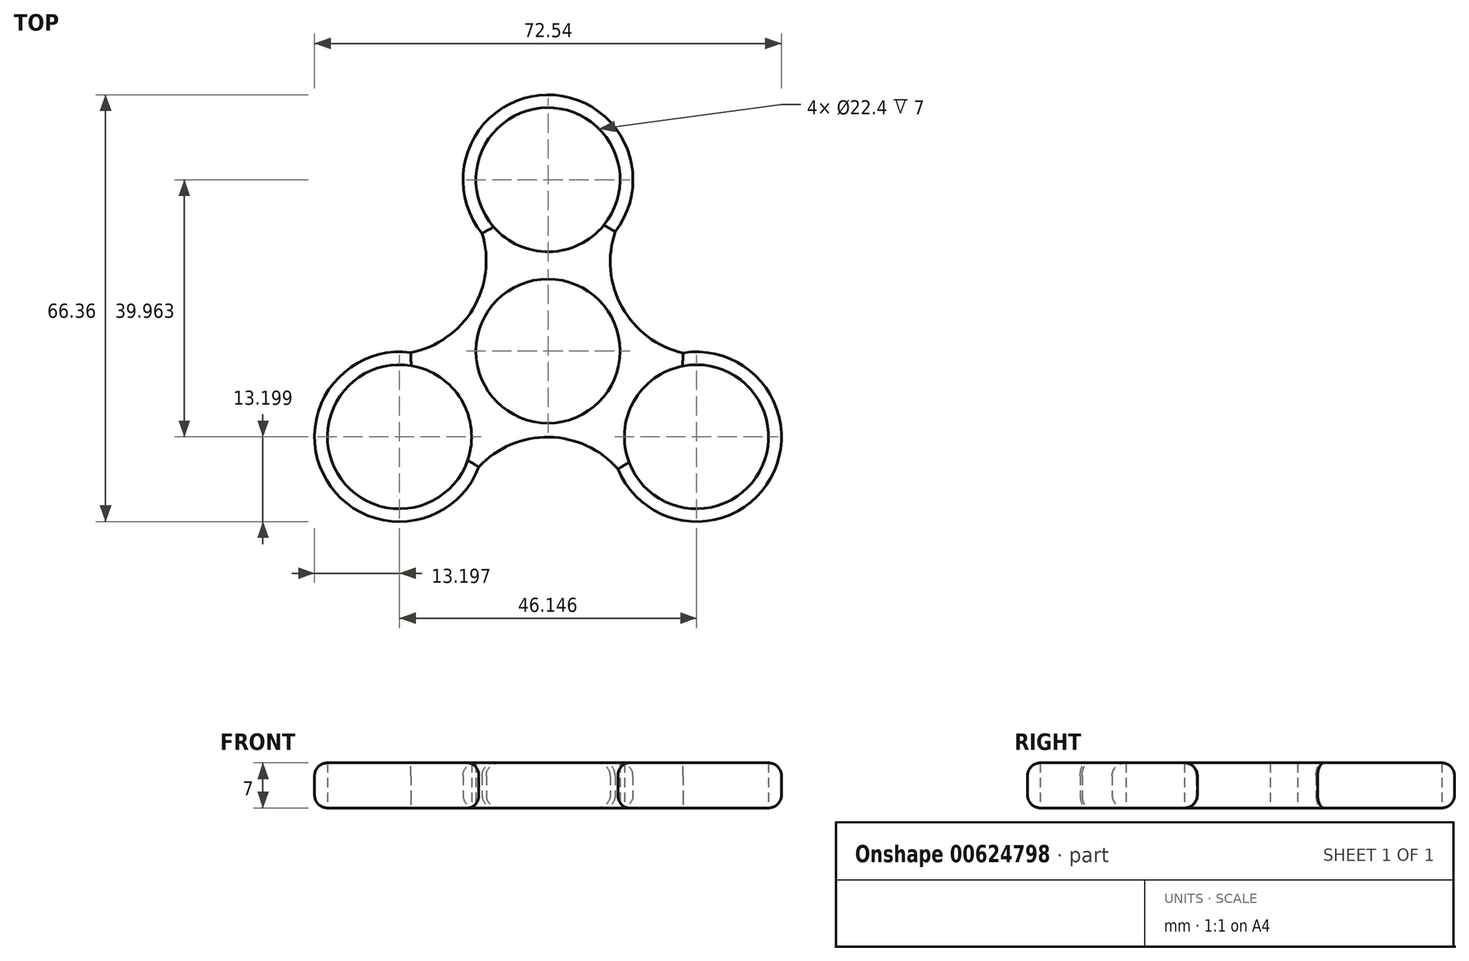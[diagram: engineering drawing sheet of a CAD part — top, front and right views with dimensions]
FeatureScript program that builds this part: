
annotation { "Feature Type Name" : "Feature", "Feature Type Description" : "" }
export const myFeature = defineFeature(function(context is Context, id is Id, definition is map)
    precondition{}
    {
        {
            var Q0;
            Q0=qCreatedBy(makeId("Top.planeOp"),FACE);
            var sketch = newSketch(context, id + "F0", { "sketchPlane" : qUnion([Q0])});
            skCircle(sketch, "E0", {"center": v(0, 0) * mm, "radius": 11.2 * mm});
            skCircle(sketch, "E1", {"center": v(0, 26.64) * mm, "radius": 11.2 * mm});
            skArc(sketch, "E2", {"start": v(10.45, 18.58) * mm, "mid": v(-0.17, 39.84) * mm, "end": v(-10.24, 18.3) * mm});
            skArc(sketch, "E3.1.0", {"start": v(-21.31, -0.24) * mm, "mid": v(-34.42, -20.07) * mm, "end": v(-10.74, -18.02) * mm});
            skCircle(sketch, "E3.1.1", {"center": v(-23.07, -13.32) * mm, "radius": 11.2 * mm});
            skArc(sketch, "E3.2.0", {"start": v(10.86, -18.34) * mm, "mid": v(34.59, -19.77) * mm, "end": v(20.98, -0.29) * mm});
            skCircle(sketch, "E3.2.1", {"center": v(23.07, -13.32) * mm, "radius": 11.2 * mm});
            skLineSegment(sketch, "E4", {"start": v(-13.37, -7.72) * mm, "end": v(-11.64, -6.72) * mm, "construction": true});
            skArc(sketch, "E5", {"start": v(10.45, 18.58) * mm, "mid": v(11.52, 6.8) * mm, "end": v(20.98, -0.29) * mm});
            skArc(sketch, "E6.1.0", {"start": v(-21.31, -0.24) * mm, "mid": v(-11.65, 6.57) * mm, "end": v(-10.24, 18.3) * mm});
            skArc(sketch, "E6.2.0", {"start": v(10.86, -18.34) * mm, "mid": v(0.13, -13.38) * mm, "end": v(-10.74, -18.02) * mm});
            skLineSegment(sketch, "E7.trimOffspring", {"start": v(11.54, 6.66) * mm, "end": v(23.07, -13.32) * mm, "construction": true});
            skLineSegment(sketch, "E8.trimOffspring", {"start": v(9.7, 5.6) * mm, "end": v(11.58, 6.69) * mm, "construction": true});
            skSolve(sketch);
        }
        {
            var Q0;
            Q0=makeQuery(id+"F0.imprint","IMPRINT",FACE,{"disambiguationData":[TD([[makeQuery(id+"F0.imprint","IMPRINT",EDGE,{"derivedFrom":sQuery(id+"F0.wireOp",EDGE,"E0")}),-1.0]])]});
            extrude(context, id + "F1", {"entities" : qUnion([Q0]), "depth" : 7 * mm, "offsetDistance" : 25 * mm});
        }
        {
            var Q0;
            Q0=makeQuery(id+"F1.opExtrude","CAP_EDGE",EDGE,{"disambiguationData":[OSD([sQuery(id+"F0.wireOp",EDGE,"E6.2.0")])],"isStart":true});
            var Q1;
            Q1=makeQuery(id+"F1.opExtrude","CAP_EDGE",EDGE,{"disambiguationData":[OSD([sQuery(id+"F0.wireOp",EDGE,"E3.2.0")])],"isStart":true});
            var Q2;
            Q2=makeQuery(id+"F1.opExtrude","CAP_EDGE",EDGE,{"disambiguationData":[OSD([sQuery(id+"F0.wireOp",EDGE,"E5")])],"isStart":true});
            var Q3;
            Q3=makeQuery(id+"F1.opExtrude","CAP_EDGE",EDGE,{"disambiguationData":[OSD([sQuery(id+"F0.wireOp",EDGE,"E2")])],"isStart":true});
            var Q4;
            Q4=makeQuery(id+"F1.opExtrude","CAP_EDGE",EDGE,{"disambiguationData":[OSD([sQuery(id+"F0.wireOp",EDGE,"E6.1.0")])],"isStart":true});
            var Q5;
            Q5=makeQuery(id+"F1.opExtrude","CAP_EDGE",EDGE,{"disambiguationData":[OSD([sQuery(id+"F0.wireOp",EDGE,"E3.1.0")])],"isStart":true});
            fillet(context, id + "F2", {"entities" : qUnion([Q0, Q1, Q2, Q3, Q4, Q5]), "radius" : 2 * mm, "tangentPropagation" : true, "allowEdgeOverflow" : false});
        }
        {
            var Q0;
            Q0=makeQuery(id+"F1.opExtrude","CAP_EDGE",EDGE,{"disambiguationData":[OSD([sQuery(id+"F0.wireOp",EDGE,"E6.1.0")])],"isStart":false});
            var Q1;
            Q1=makeQuery(id+"F1.opExtrude","CAP_EDGE",EDGE,{"disambiguationData":[OSD([sQuery(id+"F0.wireOp",EDGE,"E2")])],"isStart":false});
            var Q2;
            Q2=makeQuery(id+"F1.opExtrude","CAP_EDGE",EDGE,{"disambiguationData":[OSD([sQuery(id+"F0.wireOp",EDGE,"E5")])],"isStart":false});
            var Q3;
            Q3=makeQuery(id+"F1.opExtrude","CAP_EDGE",EDGE,{"disambiguationData":[OSD([sQuery(id+"F0.wireOp",EDGE,"E3.2.0")])],"isStart":false});
            var Q4;
            Q4=makeQuery(id+"F1.opExtrude","CAP_EDGE",EDGE,{"disambiguationData":[OSD([sQuery(id+"F0.wireOp",EDGE,"E6.2.0")])],"isStart":false});
            var Q5;
            Q5=makeQuery(id+"F1.opExtrude","CAP_EDGE",EDGE,{"disambiguationData":[OSD([sQuery(id+"F0.wireOp",EDGE,"E3.1.0")])],"isStart":false});
            fillet(context, id + "F3", {"entities" : qUnion([Q0, Q1, Q2, Q3, Q4, Q5]), "radius" : 2 * mm, "tangentPropagation" : true, "allowEdgeOverflow" : false});
        }
    });
